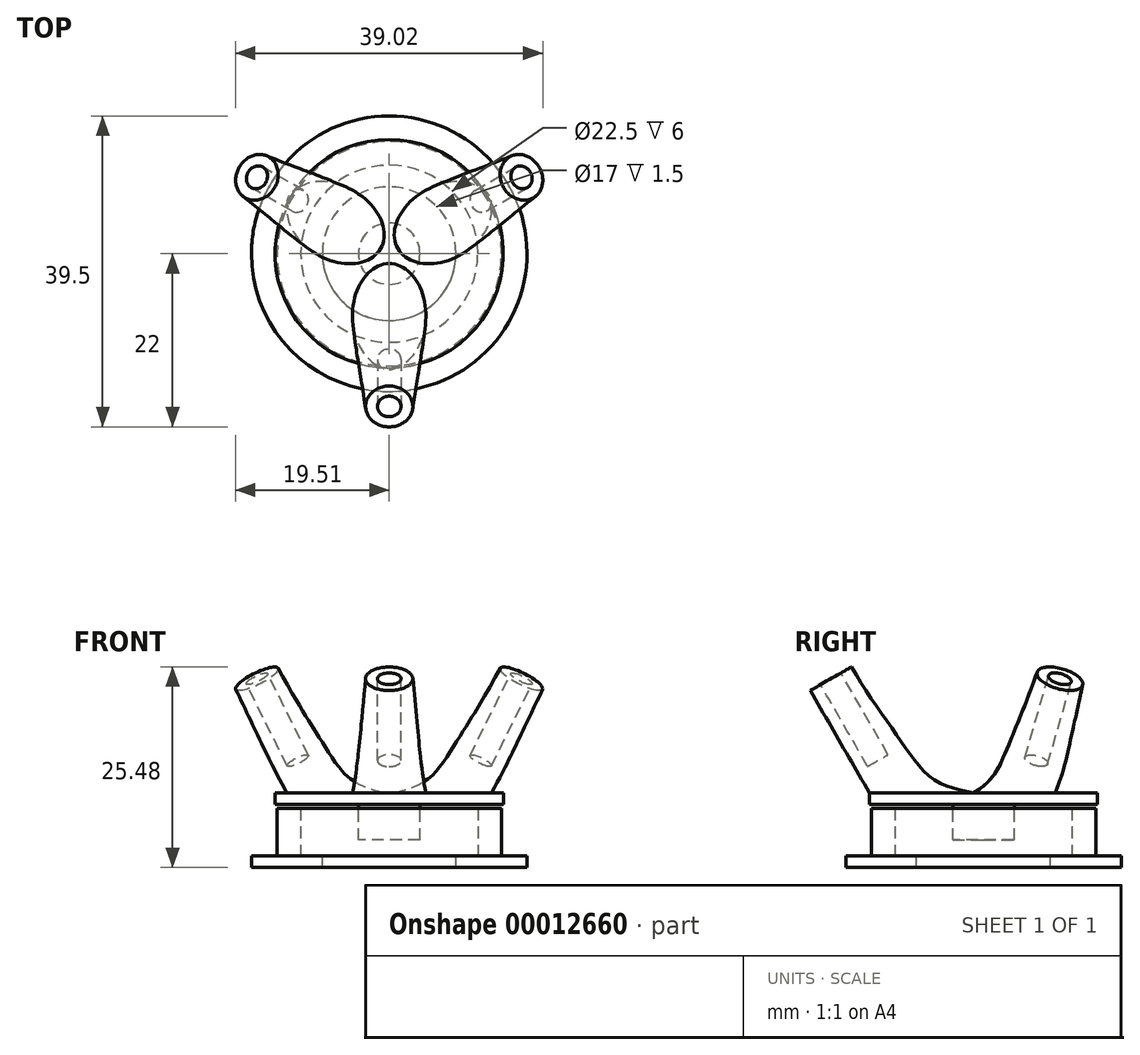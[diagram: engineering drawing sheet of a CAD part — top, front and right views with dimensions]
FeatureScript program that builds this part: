
annotation { "Feature Type Name" : "Feature", "Feature Type Description" : "" }
export const myFeature = defineFeature(function(context is Context, id is Id, definition is map)
    precondition{}
    {
        {
            var Q0;
            Q0=qCreatedBy(makeId("Top.planeOp"),FACE);
            var sketch = newSketch(context, id + "F0", { "sketchPlane" : qUnion([Q0])});
            skCircle(sketch, "E0", {"center": v(0, 0) * mm, "radius": 11.25 * mm});
            skCircle(sketch, "E1.0", {"center": v(0, 0) * mm, "radius": 14.25 * mm});
            skSolve(sketch);
        }
        {
            var Q0;
            Q0=qSketchRegion(id+"F0",true);
            extrude(context, id + "F1", {"entities" : qUnion([Q0]), "depth" : 6 * mm});
        }
        {
            var Q0;
            Q0=makeQuery(id+"F1.opExtrude","CAP_FACE",FACE,{"disambiguationData":[OSD([sQuery(id+"F0.wireOp",EDGE,"E0"),sQuery(id+"F0.wireOp",EDGE,"E1.0")])],"isStart":true});
            var sketch = newSketch(context, id + "F2", { "sketchPlane" : qUnion([Q0])});
            skCircle(sketch, "E2", {"center": v(0, 0) * mm, "radius": 17.5 * mm});
            skSolve(sketch);
        }
        {
            var Q0;
            Q0=qSketchRegion(id+"F2",true);
            extrude(context, id + "F3", {"entities" : qUnion([Q0]), "operationType" : NewBodyOperationType.ADD, "depth" : 1.5 * mm});
        }
        {
            var Q0;
            Q0=makeQuery(id+"F1.opExtrude","CAP_FACE",FACE,{"disambiguationData":[OSD([sQuery(id+"F0.wireOp",EDGE,"E0"),sQuery(id+"F0.wireOp",EDGE,"E1.0")])],"isStart":false});
            var sketch = newSketch(context, id + "F4", { "sketchPlane" : qUnion([Q0])});
            skCircle(sketch, "E3", {"center": v(0, 0) * mm, "radius": 3.9 * mm});
            skSolve(sketch);
        }
        {
            var Q0;
            Q0=qSketchRegion(id+"F4",true);
            extrude(context, id + "F5", {"entities" : qUnion([Q0]), "oppositeDirection" : true, "depth" : 4 * mm, "hasSecondDirection" : true, "secondDirectionOppositeDirection" : false, "secondDirectionDepth" : .5 * mm});
        }
        {
            var Q0;
            Q0=makeQuery(id+"F5.opExtrude","CAP_FACE",FACE,{"disambiguationData":[OSD([sQuery(id+"F4.wireOp",EDGE,"E3")])],"isStart":true});
            var sketch = newSketch(context, id + "F6", { "sketchPlane" : qUnion([Q0])});
            skCircle(sketch, "E4", {"center": v(0, 0) * mm, "radius": 14.5 * mm});
            skSolve(sketch);
        }
        {
            var Q0;
            Q0=makeQuery(id+"F6.imprint","IMPRINT",FACE,{"disambiguationData":[TD([[makeQuery(id+"F6.imprint","IMPRINT",EDGE,{"derivedFrom":makeQuery(id+"F5.opExtrude","CAP_EDGE",EDGE,{"disambiguationData":[OSD([sQuery(id+"F4.wireOp",EDGE,"E3")])],"isStart":true})}),1.0]])]});
            var Q1;
            Q1=makeQuery(id+"F6.imprint","IMPRINT",FACE,{"disambiguationData":[TD([[makeQuery(id+"F6.imprint","IMPRINT",EDGE,{"derivedFrom":sQuery(id+"F6.wireOp",EDGE,"E4")}),1.0]])]});
            extrude(context, id + "F7", {"entities" : qUnion([Q0, Q1]), "operationType" : NewBodyOperationType.ADD, "depth" : 1.5 * mm});
        }
        {
            var Q0;
            Q0=makeQuery(id+"F3.boolean.opBoolean","SPLIT",FACE,{"disambiguationData":[TD([makeQuery(id+"F1.opExtrude","SWEPT_FACE",FACE,{"disambiguationData":[OSD([sQuery(id+"F0.wireOp",EDGE,"E0")])]})])],"derivedFrom":makeQuery(id+"F3.opExtrude","CAP_FACE",FACE,{"disambiguationData":[OSD([sQuery(id+"F2.wireOp",EDGE,"E2")])],"isStart":true})});
            var sketch = newSketch(context, id + "F8", { "sketchPlane" : qUnion([Q0])});
            skCircle(sketch, "E5", {"center": v(0, 0) * mm, "radius": 8.5 * mm});
            skSolve(sketch);
        }
        {
            var Q0;
            Q0=makeQuery(id+"F8.imprint","IMPRINT",FACE,{"disambiguationData":[TD([[makeQuery(id+"F8.imprint","IMPRINT",EDGE,{"derivedFrom":sQuery(id+"F8.wireOp",EDGE,"E5")}),1.0]])]});
            extrude(context, id + "F9", {"entities" : qUnion([Q0]), "operationType" : NewBodyOperationType.REMOVE, "oppositeDirection" : true, "depth" : 5 * mm});
        }
        {
            var Q0;
            Q0=qCreatedBy(makeId("Right.planeOp"),FACE);
            var sketch = newSketch(context, id + "F10", { "sketchPlane" : qUnion([Q0])});
            skLineSegment(sketch, "E6", {"start": v(-14.5, 8) * mm, "end": v(-22, 21) * mm});
            skLineSegment(sketch, "E7.0", {"start": v(-14.5, 8) * mm, "end": v(14.5, 8) * mm, "construction": true});
            skLineSegment(sketch, "E8", {"start": v(-22, 21) * mm, "end": v(-16.8, 23.98) * mm, "construction": true});
            skFitSpline(sketch, "E9", {"points": [v(-16.8, 23.98) * mm, v(-13.9, 19.43) * mm, v(-11.07, 15.38) * mm, v(-8.97, 12.4) * mm, v(-6.78, 10.01) * mm, v(-4.19, 8.7) * mm, v(-1.26, 8) * mm], "startDerivative": vector(14.32, -23.14) * mm, "endDerivative": vector(20.06, -3.94) * mm});
            skSolve(sketch);
        }
        {
            var Q0;
            Q0=makeQuery(id+"F7.opExtrude","CAP_FACE",FACE,{"disambiguationData":[OSD([sQuery(id+"F6.wireOp",EDGE,"E4")])],"isStart":false});
            var sketch = newSketch(context, id + "F11", { "sketchPlane" : qUnion([Q0])});
            skEllipse(sketch, "E10", {"center": v(0, -7.88) * mm, "majorRadius": 6.62 * mm, "minorRadius": 4.67 * mm, "majorAxis": v(0, -1)});
            skPoint(sketch, "E11", {"position": v(0, -14.5) * mm});
            skSolve(sketch);
        }
        {
            var Q0;
            Q0=sQuery(id+"F10.wireOp",EDGE,"E8");
            cPlane(context, id + "F12", {"entities" : qUnion([Q0]), "cplaneType" : CPlaneType.LINE_ANGLE, "offset" : 150 * mm, "angle" : 0 * degree, "width" : 150 * mm, "height" : 150 * mm});
        }
        {
            var Q0;
            Q0=qCreatedBy(id+"F12.planeOp",FACE);
            var sketch = newSketch(context, id + "F13", { "sketchPlane" : qUnion([Q0])});
            skLineSegment(sketch, "E12.0", {"start": v(0, -8.62) * mm, "end": v(0, -2.61) * mm, "construction": true});
            skCircle(sketch, "E13", {"center": v(0, -5.61) * mm, "radius": 3 * mm});
            skSolve(sketch);
        }
        {
            var Q1;
            Q1=makeQuery(id+"F13.imprint","IMPRINT",FACE,{"disambiguationData":[TD([[makeQuery(id+"F13.imprint","IMPRINT",EDGE,{"derivedFrom":sQuery(id+"F13.wireOp",EDGE,"E13")}),1.0]])]});
            var Q2;
            Q2=makeQuery(id+"F11.imprint","IMPRINT",FACE,{"disambiguationData":[TD([[makeQuery(id+"F11.imprint","IMPRINT",EDGE,{"derivedFrom":sQuery(id+"F11.wireOp",EDGE,"E10")}),1.0]])]});
            var Q3;
            Q3=sQuery(id+"F10.wireOp",EDGE,"E9");
            var Q4;
            Q4=sQuery(id+"F10.wireOp",EDGE,"E6");
            loft(context, id + "F14", {"operationType" : NewBodyOperationType.ADD, "addGuides" : true, "sheetProfilesArray" : [{ "sheetProfileEntities" : qUnion([Q1]) }, { "sheetProfileEntities" : qUnion([Q2]) }], "guidesArray" : [{ "guideEntities" : qUnion([Q3]), "guideDerivativeType" : LoftGuideDerivativeType.DEFAULT, "guideDerivativeMagnitude" : 1 }, { "guideEntities" : qUnion([Q4]), "guideDerivativeType" : LoftGuideDerivativeType.DEFAULT, "guideDerivativeMagnitude" : 1 }]});
        }
        {
            var Q0;
            Q0=makeQuery(id+"F14.opLoft","CAP_FACE",FACE,{"disambiguationData":[OSD([makeQuery(id+"F13.imprint","IMPRINT",FACE,{"disambiguationData":[TD([[makeQuery(id+"F13.imprint","IMPRINT",EDGE,{"derivedFrom":sQuery(id+"F13.wireOp",EDGE,"E13")}),1.0]])]})])],"isStart":true});
            var sketch = newSketch(context, id + "F15", { "sketchPlane" : qUnion([Q0])});
            skLineSegment(sketch, "E14", {"start": v(0, -2.61) * mm, "end": v(0, -2.61) * mm});
            skCircle(sketch, "E15", {"center": v(0, -5.61) * mm, "radius": 1.5 * mm});
            skLineSegment(sketch, "E16", {"start": v(0, -8.62) * mm, "end": v(0, -2.61) * mm, "construction": true});
            skSolve(sketch);
        }
        {
            var Q0;
            Q0=makeQuery(id+"F15.imprint","IMPRINT",FACE,{"disambiguationData":[TD([[makeQuery(id+"F15.imprint","IMPRINT",EDGE,{"derivedFrom":sQuery(id+"F15.wireOp",EDGE,"E15")}),1.0]])]});
            extrude(context, id + "F16", {"entities" : qUnion([Q0]), "operationType" : NewBodyOperationType.REMOVE, "oppositeDirection" : true, "depth" : 12 * mm});
        }
        {
            var Q0;
            Q0=qCreatedBy(makeId("Front.planeOp"),FACE);
            var sketch = newSketch(context, id + "F17", { "sketchPlane" : qUnion([Q0])});
            skLineSegment(sketch, "E17", {"start": v(0, 0) * mm, "end": v(0, 36.23) * mm, "construction": true});
            skSolve(sketch);
        }
        {
            var Q0;
            Q0=makeQuery(id+"F14.opLoft","SWEPT_FACE",FACE,{"disambiguationData":[OSD([sQuery(id+"F10.wireOp",EDGE,"E6"),sQuery(id+"F10.wireOp",EDGE,"E9"),sQuery(id+"F11.wireOp",EDGE,"E10"),sQuery(id+"F13.wireOp",EDGE,"E13")])]});
            var Q1;
            Q1=makeQuery(id+"F16.boolean.opBoolean","COPY",FACE,{"derivedFrom":makeQuery(id+"F16.opExtrude","SWEPT_FACE",FACE,{"disambiguationData":[OSD([sQuery(id+"F15.wireOp",EDGE,"E15")])]})});
            var Q2;
            Q2=makeQuery(id+"F14.opLoft","CAP_FACE",FACE,{"disambiguationData":[OSD([makeQuery(id+"F13.imprint","IMPRINT",FACE,{"disambiguationData":[TD([[makeQuery(id+"F13.imprint","IMPRINT",EDGE,{"derivedFrom":sQuery(id+"F13.wireOp",EDGE,"E13")}),1.0]])]})])],"isStart":true});
            var Q3;
            Q3=makeQuery(id+"F16.boolean.opBoolean","COPY",FACE,{"derivedFrom":makeQuery(id+"F16.opExtrude","CAP_FACE",FACE,{"disambiguationData":[OSD([sQuery(id+"F15.wireOp",EDGE,"E15")])],"isStart":false})});
            var Q4;
            Q4=sQuery(id+"F17.wireOp",EDGE,"E17");
            circularPattern(context, id + "F18", {"faces" : qUnion([Q0, Q1, Q2, Q3]), "axis" : qUnion([Q4]), "angle" : 360 * degree, "instanceCount" : 3, "equalSpace" : true, "patternType" : PatternType.FACE});
        }
    });
